AUTODESK INVENTOR PART (.ipt)
format: ipt  version: 2017 (Build 210142000, 142)  size: 109,056 bytes
history: native  units: in
note: dims shown in document units (in); Inventor stores cm internally (conversion verified against a paired STEP export)
features: sketch x3, other x3, extrude x2, plane x1
ambient origin geometry x8: Origin, YZ Plane, XZ Plane, XY Plane, X Axis, Y Axis, Z Axis, Center Point
bodies: Solid1 (feature_tree)
feature tree (9):
  extrude  "Extrusion1"  Depth=0.1575in
  sketch  "Sketch2"  dims[d2=0.315in d3=0.0in d4=5.2362in]
  plane  "Work Plane2"
  extrude  "Extrusion2"  Depth=5.2362in
  sketch  "Sketch1"  dims[d0=1.1811in d1=0.1575in]
  sketch  "Sketch4"  dims[d5=2.5591in d6=0.0787in d7=0.0in]
  other  "<userpath>\Desktop\Current-Meter-Pcb-Fall-16-master\CAD\DesigningTop.iam"
  other  "DesigningTop.iam"
  other  "case3:1"
